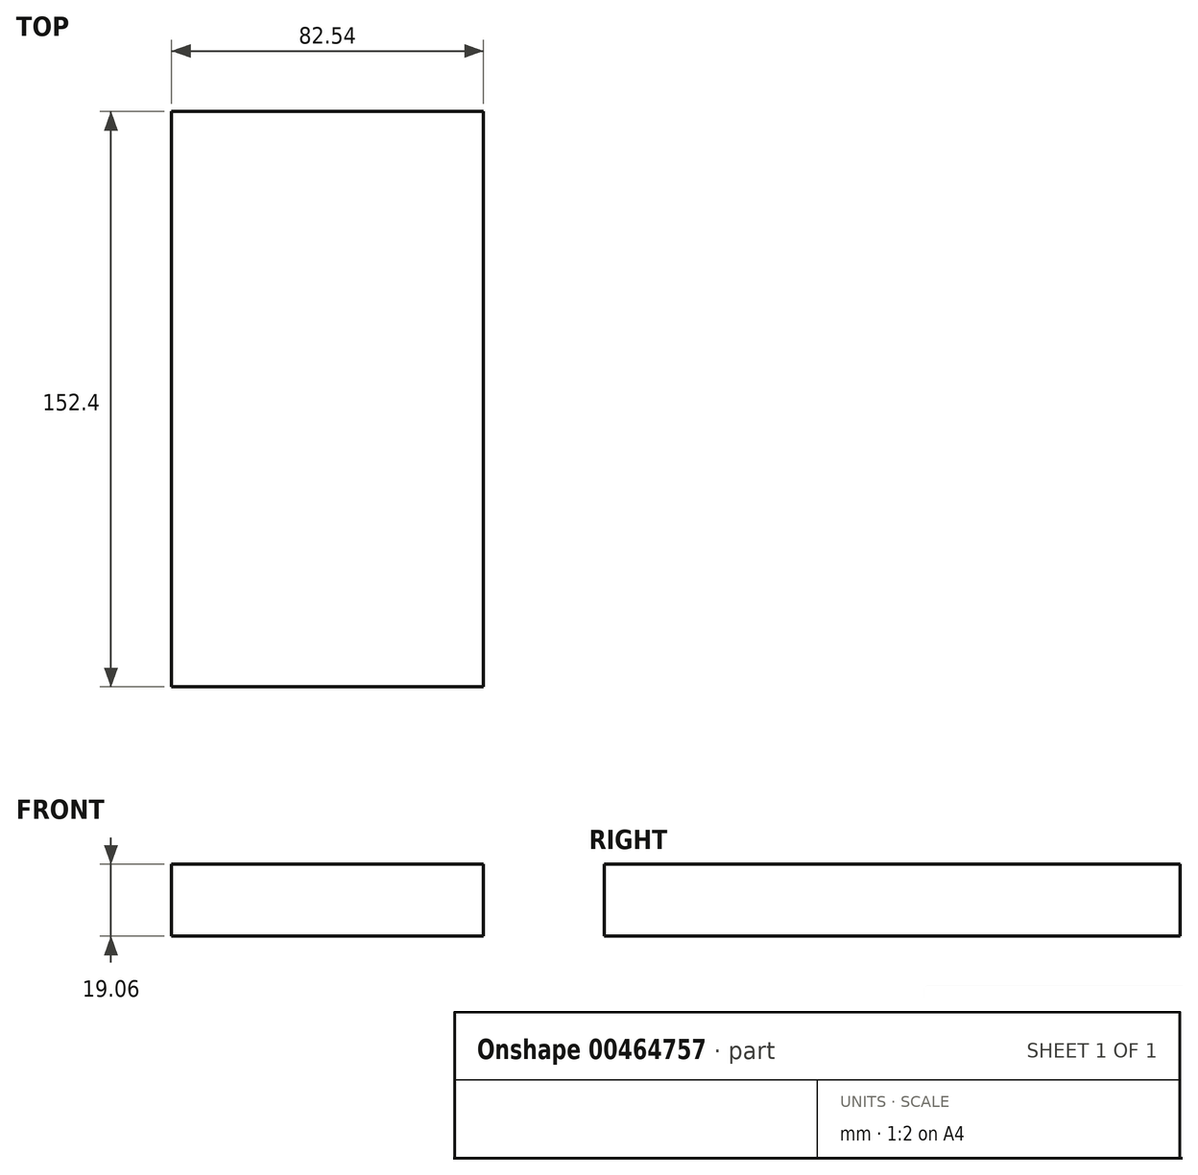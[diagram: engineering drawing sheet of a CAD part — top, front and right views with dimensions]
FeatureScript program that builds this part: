
annotation { "Feature Type Name" : "Feature", "Feature Type Description" : "" }
export const myFeature = defineFeature(function(context is Context, id is Id, definition is map)
    precondition{}
    {
        {
            var Q0;
            Q0=qCreatedBy(makeId("Front.planeOp"),FACE);
            var sketch = newSketch(context, id + "F0", { "sketchPlane" : qUnion([Q0])});
            skLineSegment(sketch, "E0.bottom", {"start": v(-41.28, 9.52) * mm, "end": v(41.28, 9.53) * mm});
            skLineSegment(sketch, "E0.top", {"start": v(-41.28, -9.53) * mm, "end": v(41.28, -9.53) * mm});
            skLineSegment(sketch, "E0.left", {"start": v(-41.28, 9.52) * mm, "end": v(-41.27, -9.53) * mm});
            skLineSegment(sketch, "E0.right", {"start": v(41.28, 9.53) * mm, "end": v(41.28, -9.52) * mm});
            skPoint(sketch, "E0.middle", {"position": v(0, 0) * mm});
            skLineSegment(sketch, "E1.bottom", {"start": v(60.32, 38.1) * mm, "end": v(111.12, 38.1) * mm});
            skLineSegment(sketch, "E1.top", {"start": v(60.32, 66.67) * mm, "end": v(111.12, 66.67) * mm});
            skLineSegment(sketch, "E1.left", {"start": v(60.32, 38.1) * mm, "end": v(60.32, 66.67) * mm});
            skLineSegment(sketch, "E1.right", {"start": v(111.12, 38.1) * mm, "end": v(111.12, 66.67) * mm});
            skPoint(sketch, "E1.middle", {"position": v(85.72, 52.39) * mm});
            skLineSegment(sketch, "E2", {"start": v(41.27, 9.53) * mm, "end": v(41.27, 28.77) * mm});
            skArc(sketch, "E3", {"start": v(41.28, 28.77) * mm, "mid": v(45.92, 40) * mm, "end": v(57.15, 44.64) * mm});
            skArc(sketch, "E4.1", {"start": v(25.78, 28.77) * mm, "mid": v(34.97, 50.95) * mm, "end": v(57.15, 60.13) * mm});
            skLineSegment(sketch, "E4.2", {"start": v(25.78, 9.53) * mm, "end": v(25.78, 28.77) * mm});
            skLineSegment(sketch, "E5", {"start": v(85.7, 60.13) * mm, "end": v(85.75, 44.64) * mm});
            skLineSegment(sketch, "E6", {"start": v(57.15, 60.13) * mm, "end": v(85.7, 60.13) * mm});
            skLineSegment(sketch, "E7", {"start": v(57.15, 44.64) * mm, "end": v(85.75, 44.64) * mm});
            skFitSpline(sketch, "E8", {"points": [v(-41.28, 9.52) * mm, v(57.15, 60.13) * mm], "startDerivative": vector(-2.12, 90.5) * mm, "endDerivative": vector(129.47, -1.22) * mm});
            skSolve(sketch);
        }
        {
            var Q0;
            Q0=makeQuery(id+"F0.imprint","IMPRINT",FACE,{"disambiguationData":[TD([[makeQuery(id+"F0.imprint","IMPRINT",EDGE,{"derivedFrom":sQuery(id+"F0.wireOp",EDGE,"E0.top")}),1.0]])]});
            var Q1;
            Q1=sQuery(id+"F0.wireOp",EDGE,"E0.top");
            var Q2;
            Q2=sQuery(id+"F0.wireOp",EDGE,"E0.bottom");
            var Q3;
            Q3=sQuery(id+"F0.wireOp",EDGE,"E0.left");
            var Q4;
            Q4=sQuery(id+"F0.wireOp",EDGE,"E0.right");
            extrude(context, id + "F1", {"entities" : qUnion([Q0]), "surfaceEntities" : qUnion([Q1, Q2, Q3, Q4]), "endBound" : BoundingType.SYMMETRIC, "depth" : 152.4 * mm});
        }
    });
